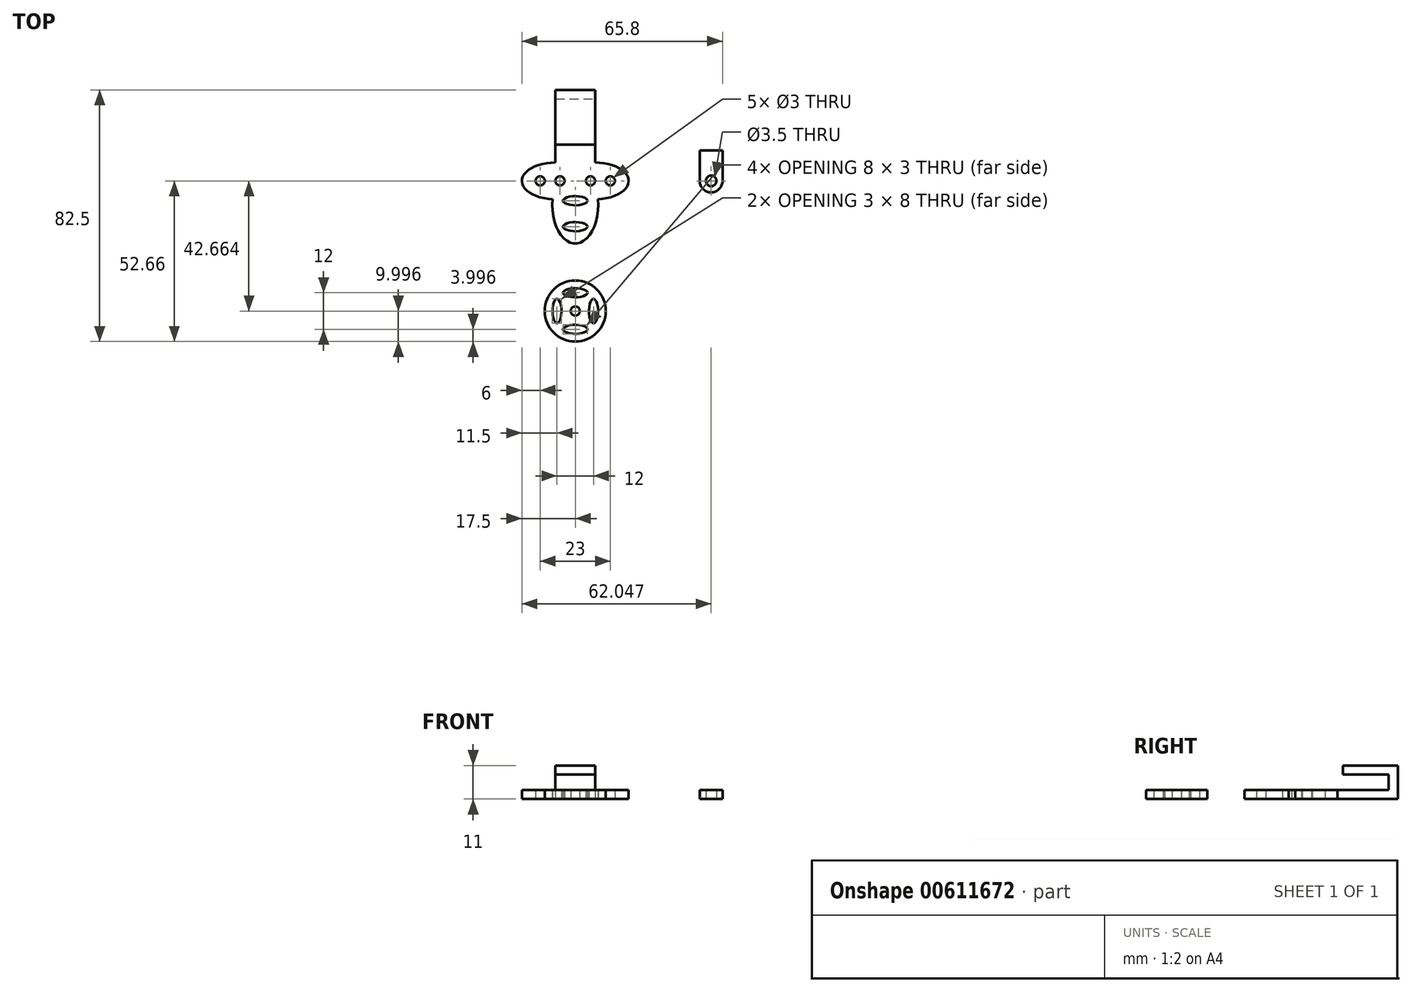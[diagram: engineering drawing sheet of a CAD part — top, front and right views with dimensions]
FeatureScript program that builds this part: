
annotation { "Feature Type Name" : "Feature", "Feature Type Description" : "" }
export const myFeature = defineFeature(function(context is Context, id is Id, definition is map)
    precondition{}
    {
        {
            var Q0;
            Q0=qCreatedBy(makeId("Top.planeOp"),FACE);
            var sketch = newSketch(context, id + "F0", { "sketchPlane" : qUnion([Q0])});
            skEllipse(sketch, "E0", {"center": v(0, 0) * mm, "majorRadius": 4 * mm, "minorRadius": 1.5 * mm, "majorAxis": v(-1, 0)});
            skLineSegment(sketch, "E1", {"start": v(0, 1.5) * mm, "end": v(0, 6.5) * mm, "construction": true});
            skLineSegment(sketch, "E2", {"start": v(0, 6.5) * mm, "end": v(5, 6.5) * mm, "construction": true});
            skLineSegment(sketch, "E3", {"start": v(0, 6.5) * mm, "end": v(-5, 6.5) * mm, "construction": true});
            skLineSegment(sketch, "E4", {"start": v(0, -1.5) * mm, "end": v(0, -8.5) * mm, "construction": true});
            skEllipse(sketch, "E5", {"center": v(0, -8.5) * mm, "majorRadius": 4 * mm, "minorRadius": 1.5 * mm, "majorAxis": v(-1, 0)});
            skEllipse(sketch, "E6", {"center": v(5, 6.5) * mm, "majorRadius": 1.5 * mm, "minorRadius": 1.5 * mm, "majorAxis": v(0, 1)});
            skEllipse(sketch, "E7", {"center": v(-5, 6.5) * mm, "majorRadius": 1.5 * mm, "minorRadius": 1.5 * mm, "majorAxis": v(0, 1)});
            skLineSegment(sketch, "E8", {"start": v(6.5, 6.5) * mm, "end": v(11.5, 6.5) * mm, "construction": true});
            skLineSegment(sketch, "E9", {"start": v(-6.5, 6.5) * mm, "end": v(-11.5, 6.5) * mm, "construction": true});
            skEllipse(sketch, "E10", {"center": v(-11.5, 6.5) * mm, "majorRadius": 1.5 * mm, "minorRadius": 1.5 * mm, "majorAxis": v(0, 1)});
            skEllipse(sketch, "E11", {"center": v(11.5, 6.5) * mm, "majorRadius": 1.5 * mm, "minorRadius": 1.5 * mm, "majorAxis": v(0, 1)});
            skEllipticalArc(sketch, "E12", {});
            skEllipticalArc(sketch, "E13", {});
            skEllipticalArc(sketch, "E14", {});
            skPoint(sketch, "E15", {"position": v(-6.5, 11.34) * mm});
            skPoint(sketch, "E16", {"position": v(6.5, 11.34) * mm});
            skLineSegment(sketch, "E17", {"start": v(-6.5, 11.34) * mm, "end": v(-6.5, 36.34) * mm});
            skLineSegment(sketch, "E18", {"start": v(6.5, 11.34) * mm, "end": v(6.5, 36.34) * mm});
            skLineSegment(sketch, "E19", {"start": v(6.5, 36.34) * mm, "end": v(-6.5, 36.34) * mm});
            skPoint(sketch, "E20", {"position": v(-6.5, 33.34) * mm});
            skLineSegment(sketch, "E21", {"start": v(-6.5, 33.34) * mm, "end": v(6.5, 33.34) * mm});
            skPoint(sketch, "E22", {"position": v(-6.5, 18.34) * mm});
            skLineSegment(sketch, "E23", {"start": v(-6.5, 18.34) * mm, "end": v(6.5, 18.34) * mm});
            skEllipse(sketch, "E24", {"center": v(0, -30.16) * mm, "majorRadius": 4 * mm, "minorRadius": 1.5 * mm, "majorAxis": v(1, 0)});
            skPoint(sketch, "E25", {"position": v(0, -36.16) * mm});
            skEllipse(sketch, "E26.1.0", {"center": v(-6, -36.16) * mm, "majorRadius": 4 * mm, "minorRadius": 1.5 * mm, "majorAxis": v(0, 1)});
            skEllipse(sketch, "E26.2.0", {"center": v(0, -42.16) * mm, "majorRadius": 4 * mm, "minorRadius": 1.5 * mm, "majorAxis": v(-1, 0)});
            skEllipse(sketch, "E26.3.0", {"center": v(6, -36.16) * mm, "majorRadius": 4 * mm, "minorRadius": 1.5 * mm, "majorAxis": v(0, -1)});
            skCircle(sketch, "E27", {"center": v(0, -36.16) * mm, "radius": 10 * mm});
            skCircle(sketch, "E28", {"center": v(0, -36.16) * mm, "radius": 1.5 * mm});
            skCircle(sketch, "E29", {"center": v(44.55, 6.5) * mm, "radius": 1.75 * mm});
            skCircle(sketch, "E30", {"center": v(44.55, 6.5) * mm, "radius": 3.75 * mm});
            skPoint(sketch, "E31", {"position": v(40.8, 6.5) * mm});
            skPoint(sketch, "E32", {"position": v(48.3, 6.5) * mm});
            skLineSegment(sketch, "E33", {"start": v(40.8, 6.5) * mm, "end": v(40.8, 16.5) * mm});
            skLineSegment(sketch, "E34", {"start": v(40.8, 16.5) * mm, "end": v(48.3, 16.5) * mm});
            skLineSegment(sketch, "E35", {"start": v(48.3, 16.5) * mm, "end": v(48.3, 6.5) * mm});
            const initialGuessF0  = {"E12": [-0.0065, 0.0065, 1, 0, 0.011, 0.006, 0.9386110781141537, 4.630351085034827], "E13": [0.0065, 0.0065, 1, 0, 0.011, 0.006, 4.794426875734552, 2.202981575475645], "E14": [0, -0.0015, 0, -1, 0.0125, 0.0075, 4.550062694663231, 1.7331226125163544]};
            skSetInitialGuess(sketch, initialGuessF0);
            skSolve(sketch);
        }
        {
            var Q0;
            Q0=makeQuery(id+"F0.imprint","IMPRINT",FACE,{"disambiguationData":[TD([[makeQuery(id+"F0.imprint","IMPRINT",EDGE,{"derivedFrom":sQuery(id+"F0.wireOp",EDGE,"E0")}),-1.0]])]});
            var Q1;
            {var subQ3=sQuery(id+"F0.wireOp",EDGE,"E23");Q1=makeQuery(id+"F0.imprint","IMPRINT",FACE,{"disambiguationData":[TD([[makeQuery(id+"F0.imprint","IMPRINT",EDGE,{"derivedFrom":subQ3}),-1.0]])]});}
            var Q2;
            {var subQ0=sQuery(id+"F0.wireOp",EDGE,"E21");Q2=makeQuery(id+"F0.imprint","IMPRINT",FACE,{"disambiguationData":[TD([[makeQuery(id+"F0.imprint","IMPRINT",EDGE,{"derivedFrom":subQ0}),-1.0]])]});}
            var Q3;
            {var subQ0=sQuery(id+"F0.wireOp",EDGE,"E19");Q3=makeQuery(id+"F0.imprint","IMPRINT",FACE,{"disambiguationData":[TD([[makeQuery(id+"F0.imprint","IMPRINT",EDGE,{"derivedFrom":subQ0}),1.0]])]});}
            extrude(context, id + "F1", {"entities" : qUnion([Q0, Q1, Q2, Q3]), "depth" : 3 * mm, "offsetDistance" : 25 * mm});
        }
        {
            var Q0;
            {var subQ0=sQuery(id+"F0.wireOp",EDGE,"E19");Q0=makeQuery(id+"F0.imprint","IMPRINT",FACE,{"disambiguationData":[TD([[makeQuery(id+"F0.imprint","IMPRINT",EDGE,{"derivedFrom":subQ0}),1.0]])]});}
            extrude(context, id + "F2", {"entities" : qUnion([Q0]), "operationType" : NewBodyOperationType.ADD, "depth" : 11 * mm, "offsetDistance" : 25 * mm});
        }
        {
            var Q0;
            {var subQ0=sQuery(id+"F0.wireOp",EDGE,"E19");Q0=makeQuery(id+"F0.imprint","IMPRINT",FACE,{"disambiguationData":[TD([[makeQuery(id+"F0.imprint","IMPRINT",EDGE,{"derivedFrom":subQ0}),1.0]])]});}
            var Q1;
            {var subQ0=sQuery(id+"F0.wireOp",EDGE,"E21");Q1=makeQuery(id+"F0.imprint","IMPRINT",FACE,{"disambiguationData":[TD([[makeQuery(id+"F0.imprint","IMPRINT",EDGE,{"derivedFrom":subQ0}),-1.0]])]});}
            extrude(context, id + "F3", {"entities" : qUnion([Q0, Q1]), "operationType" : NewBodyOperationType.ADD, "depth" : 11 * mm, "offsetDistance" : 25 * mm, "hasSecondDirection" : true, "secondDirectionOppositeDirection" : false, "secondDirectionDepth" : 8 * mm});
        }
        {
            var Q0;
            Q0=makeQuery(id+"F0.imprint","IMPRINT",FACE,{"disambiguationData":[TD([[makeQuery(id+"F0.imprint","IMPRINT",EDGE,{"derivedFrom":sQuery(id+"F0.wireOp",EDGE,"E24")}),-1.0]])]});
            extrude(context, id + "F4", {"entities" : qUnion([Q0]), "depth" : 3 * mm, "offsetDistance" : 25 * mm});
        }
        {
            var Q0;
            {var subQ0=sQuery(id+"F0.wireOp",EDGE,"E33");Q0=makeQuery(id+"F0.imprint","IMPRINT",FACE,{"disambiguationData":[TD([[makeQuery(id+"F0.imprint","IMPRINT",EDGE,{"derivedFrom":subQ0}),-1.0]])]});}
            var Q1;
            Q1=makeQuery(id+"F0.imprint","IMPRINT",FACE,{"disambiguationData":[TD([[makeQuery(id+"F0.imprint","IMPRINT",EDGE,{"derivedFrom":sQuery(id+"F0.wireOp",EDGE,"E29")}),-1.0]])]});
            extrude(context, id + "F5", {"entities" : qUnion([Q0, Q1]), "depth" : 3 * mm, "offsetDistance" : 25 * mm});
        }
    });
